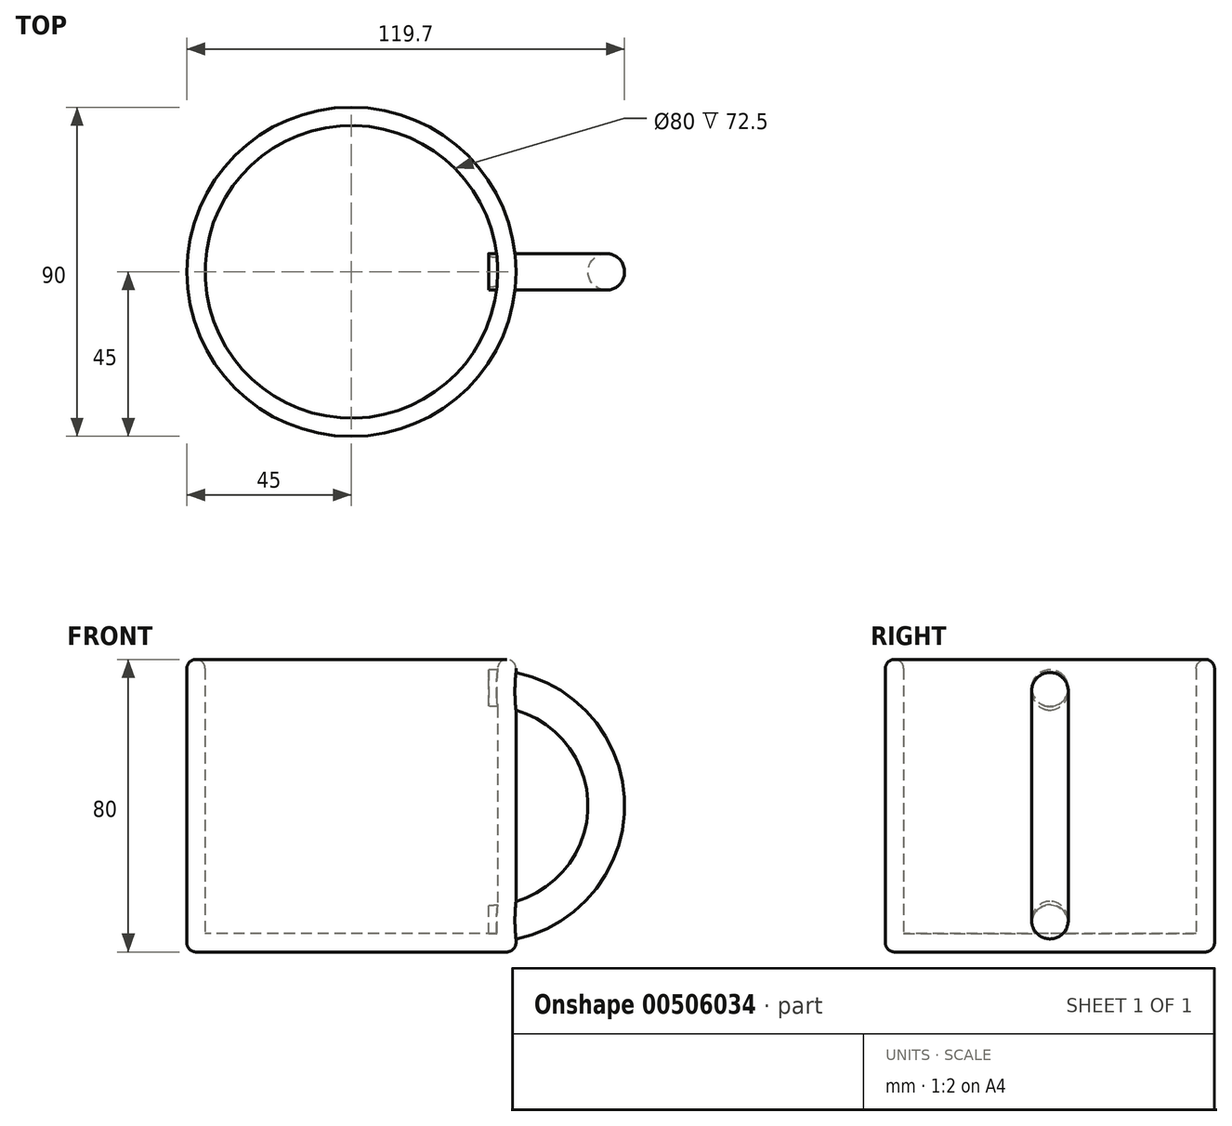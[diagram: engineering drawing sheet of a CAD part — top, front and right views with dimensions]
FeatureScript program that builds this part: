
annotation { "Feature Type Name" : "Feature", "Feature Type Description" : "" }
export const myFeature = defineFeature(function(context is Context, id is Id, definition is map)
    precondition{}
    {
        {
            var Q0;
            Q0=qCreatedBy(makeId("Top.planeOp"),FACE);
            var sketch = newSketch(context, id + "F0", { "sketchPlane" : qUnion([Q0])});
            skCircle(sketch, "E0", {"center": v(0, 0) * mm, "radius": 45 * mm});
            skSolve(sketch);
        }
        {
            var Q0;
            Q0=makeQuery(id+"F0.imprint","IMPRINT",FACE,{"disambiguationData":[TD([[makeQuery(id+"F0.imprint","IMPRINT",EDGE,{"derivedFrom":sQuery(id+"F0.wireOp",EDGE,"E0")}),1.0]])]});
            extrude(context, id + "F1", {"entities" : qUnion([Q0]), "depth" : 80 * mm});
        }
        {
            var Q0;
            Q0=makeQuery(id+"F1.opExtrude","CAP_FACE",FACE,{"disambiguationData":[OSD([sQuery(id+"F0.wireOp",EDGE,"E0")])],"isStart":false});
            shell(context, id + "F2", {"entities" : qUnion([Q0]), "thickness" : 5 * mm});
        }
        {
            var Q0;
            Q0=qCreatedBy(makeId("Right.planeOp"),FACE);
            cPlane(context, id + "F3", {"entities" : qUnion([Q0]), "cplaneType" : CPlaneType.OFFSET, "offset" : 37.5 * mm, "width" : 150 * mm, "height" : 150 * mm});
        }
        {
            var Q0;
            Q0=qCreatedBy(id+"F3.planeOp",FACE);
            var sketch = newSketch(context, id + "F4", { "sketchPlane" : qUnion([Q0])});
            skCircle(sketch, "E1", {"center": v(0, 72.2) * mm, "radius": 5 * mm});
            skLineSegment(sketch, "E2", {"start": v(0, 40) * mm, "end": v(72.39, 40) * mm});
            skSolve(sketch);
        }
        {
            var Q0;
            Q0 = qSketchRegion(id + "F4", true);
            var Q1;
            Q1=sQuery(id+"F4.wireOp",EDGE,"E2");
            revolve(context, id + "F5", {"operationType" : NewBodyOperationType.ADD, "entities" : qUnion([Q0]), "axis" : qUnion([Q1]), "revolveType" : RevolveType.ONE_DIRECTION, "angle" : 180 * degree});
        }
        {
            var Q0;
            Q0=makeQuery(id+"F1.opExtrude","CAP_EDGE",EDGE,{"disambiguationData":[OSD([sQuery(id+"F0.wireOp",EDGE,"E0")])],"isStart":false});
            var Q1;
            {var subQ0=sQuery(id+"F0.wireOp",EDGE,"E0");Q1=makeQuery(id+"F2.opShell","OFFSET_EDGE",EDGE,{"disambiguationData":[OSD([subQ0]),TDD([makeQuery(id+"F1.opExtrude","CAP_EDGE",EDGE,{"disambiguationData":[OSD([subQ0])],"isStart":false})])]});}
            var Q2;
            Q2=makeQuery(id+"F1.opExtrude","CAP_EDGE",EDGE,{"disambiguationData":[OSD([sQuery(id+"F0.wireOp",EDGE,"E0")])],"isStart":true});
            fillet(context, id + "F6", {"entities" : qUnion([Q0, Q1, Q2]), "radius" : 2.5 * mm, "tangentPropagation" : true, "allowEdgeOverflow" : false});
        }
    });
